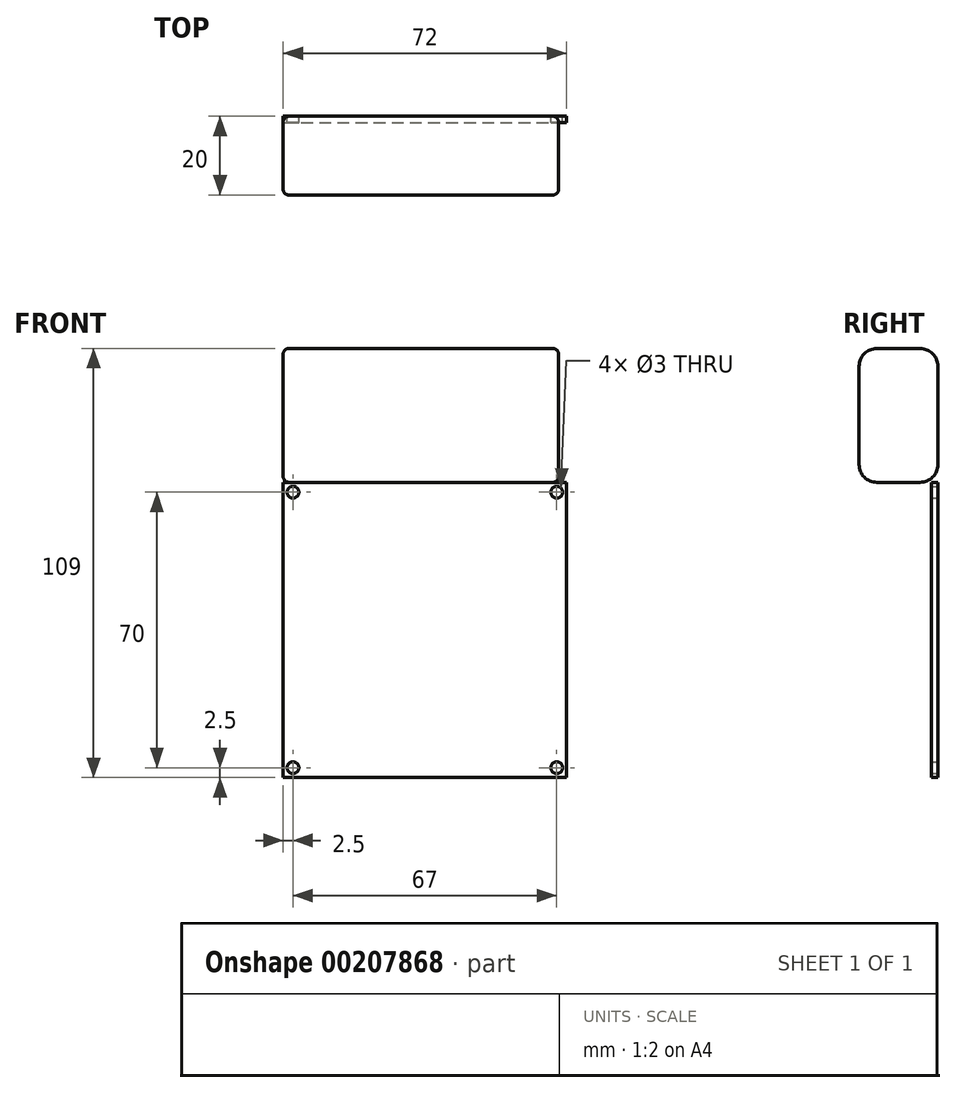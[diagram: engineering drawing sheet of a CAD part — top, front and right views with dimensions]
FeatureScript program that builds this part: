
annotation { "Feature Type Name" : "Feature", "Feature Type Description" : "" }
export const myFeature = defineFeature(function(context is Context, id is Id, definition is map)
    precondition{}
    {
        {
            var Q0;
            Q0=qCreatedBy(makeId("Front.planeOp"),FACE);
            var sketch = newSketch(context, id + "F0", { "sketchPlane" : qUnion([Q0])});
            skLineSegment(sketch, "E0.bottom", {"start": v(0, 0) * mm, "end": v(72, 0) * mm});
            skLineSegment(sketch, "E0.top", {"start": v(0, -75) * mm, "end": v(72, -75) * mm});
            skLineSegment(sketch, "E0.left", {"start": v(0, 0) * mm, "end": v(0, -75) * mm});
            skLineSegment(sketch, "E0.right", {"start": v(72, 0) * mm, "end": v(72, -75) * mm});
            skLineSegment(sketch, "E1.bottom", {"start": v(2.5, -2.5) * mm, "end": v(69.5, -2.5) * mm, "construction": true});
            skLineSegment(sketch, "E1.top", {"start": v(2.5, -72.5) * mm, "end": v(69.5, -72.5) * mm, "construction": true});
            skLineSegment(sketch, "E1.left", {"start": v(2.5, -2.5) * mm, "end": v(2.5, -72.5) * mm, "construction": true});
            skLineSegment(sketch, "E1.right", {"start": v(69.5, -2.5) * mm, "end": v(69.5, -72.5) * mm, "construction": true});
            skLineSegment(sketch, "E2", {"start": v(36, -2.5) * mm, "end": v(36, 0) * mm, "construction": true});
            skLineSegment(sketch, "E3", {"start": v(2.5, -37.5) * mm, "end": v(0, -37.5) * mm, "construction": true});
            skPoint(sketch, "E3.endSnap0", {"position": v(2.5, -37.5) * mm});
            skCircle(sketch, "E4", {"center": v(2.5, -2.5) * mm, "radius": 1.5 * mm});
            skCircle(sketch, "E5", {"center": v(69.5, -2.5) * mm, "radius": 1.5 * mm});
            skCircle(sketch, "E6", {"center": v(69.5, -72.5) * mm, "radius": 1.5 * mm});
            skCircle(sketch, "E7", {"center": v(2.5, -72.5) * mm, "radius": 1.5 * mm});
            skSolve(sketch);
        }
        {
            var Q0;
            Q0 = qSketchRegion(id + "F0", true);
            extrude(context, id + "F1", {"entities" : qUnion([Q0]), "depth" : 1.6 * mm});
        }
        {
            var Q0;
            Q0=qCreatedBy(makeId("Front.planeOp"),FACE);
            var sketch = newSketch(context, id + "F2", { "sketchPlane" : qUnion([Q0])});
            skLineSegment(sketch, "E8.bottom", {"start": v(0, 0) * mm, "end": v(70, 0) * mm});
            skLineSegment(sketch, "E8.top", {"start": v(0, 34) * mm, "end": v(70, 34) * mm});
            skLineSegment(sketch, "E8.left", {"start": v(0, 0) * mm, "end": v(0, 34) * mm});
            skLineSegment(sketch, "E8.right", {"start": v(70, 0) * mm, "end": v(70, 34) * mm});
            skSolve(sketch);
        }
        {
            var Q0;
            Q0=makeQuery(id+"F2.imprint","IMPRINT",FACE,{"disambiguationData":[TD([[makeQuery(id+"F2.imprint","IMPRINT",EDGE,{"derivedFrom":sQuery(id+"F2.wireOp",EDGE,"E8.bottom")}),1.0]])]});
            extrude(context, id + "F3", {"entities" : qUnion([Q0]), "depth" : 20 * mm});
        }
        {
            var Q0;
            Q0=makeQuery(id+"F3.opExtrude","SWEPT_FACE",FACE,{"disambiguationData":[OSD([sQuery(id+"F2.wireOp",EDGE,"E8.right")])]});
            var Q1;
            Q1=makeQuery(id+"F3.opExtrude","SWEPT_FACE",FACE,{"disambiguationData":[OSD([sQuery(id+"F2.wireOp",EDGE,"E8.left")])]});
            fillet(context, id + "F4", {"entities" : qUnion([Q0, Q1]), "radius" : 1.5 * mm, "tangentPropagation" : true, "allowEdgeOverflow" : false});
        }
        {
            var Q0;
            Q0=makeQuery(id+"F3.opExtrude","CAP_EDGE",EDGE,{"disambiguationData":[OSD([sQuery(id+"F2.wireOp",EDGE,"E8.top")])],"isStart":true});
            var Q1;
            Q1=makeQuery(id+"F3.opExtrude","CAP_EDGE",EDGE,{"disambiguationData":[OSD([sQuery(id+"F2.wireOp",EDGE,"E8.bottom")])],"isStart":true});
            var Q2;
            Q2=makeQuery(id+"F3.opExtrude","CAP_EDGE",EDGE,{"disambiguationData":[OSD([sQuery(id+"F2.wireOp",EDGE,"E8.top")])],"isStart":false});
            var Q3;
            Q3=makeQuery(id+"F3.opExtrude","CAP_EDGE",EDGE,{"disambiguationData":[OSD([sQuery(id+"F2.wireOp",EDGE,"E8.bottom")])],"isStart":false});
            fillet(context, id + "F5", {"entities" : qUnion([Q0, Q1, Q2, Q3]), "radius" : 4.5 * mm, "tangentPropagation" : true, "allowEdgeOverflow" : false});
        }
    });
